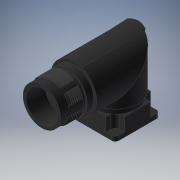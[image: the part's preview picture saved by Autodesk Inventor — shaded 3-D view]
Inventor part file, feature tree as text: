
AUTODESK INVENTOR PART (.ipt)
format: ipt  version: 2019 (Build 230136000, 136)  size: 380,928 bytes
history: native  units: mm
features: other x7, extrude x4, revolve x3
ambient origin geometry x8: Origin, YZ Plane, XZ Plane, XY Plane, X Axis, Y Axis, Z Axis, Center Point
bodies: Solid1 (feature_tree)
feature tree (14):
  extrude  "Extrusion1"  Depth=10.2mm TaperAngle=0.0deg
  extrude  "Extrusion2"  Depth=7.7mm TaperAngle=0.0deg
  revolve  "Revolution1"  Angle=360.0deg
  revolve  "Revolution2"  Angle=360.0deg
  revolve  "Revolution3"  [1 undecoded]
  extrude  "Extrusion3"  Depth=40.0mm TaperAngle=0.0deg
  extrude  "Extrusion4"  Depth=13.2mm TaperAngle=0.0deg
  other  "to_XY"
  other  "to_YZ"
  other  "to_ZX"
  other  "to_X"
  other  "to_Y"
  other  "to_Z"
  other  "to_Center"
note: 1 required parameter value undecoded (feature->parameter linkage not recoverable at this tier; creation-order binding heuristic only, values carry confidence <= 0.55)
